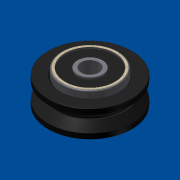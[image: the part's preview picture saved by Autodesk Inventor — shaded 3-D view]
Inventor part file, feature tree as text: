
AUTODESK INVENTOR PART (.ipt)
format: ipt  version: 2013 (Build 170138000, 138)  size: 254,464 bytes
history: native  units: in
note: dims shown in document units (in); Inventor stores cm internally (conversion verified against a paired STEP export)
features: other x6, extrude x2, sketch x2
ambient origin geometry x8: Origin, YZ Plane, XZ Plane, XY Plane, X Axis, Y Axis, Z Axis, Center Point
bodies: Solid1 (feature_tree)
feature tree (10):
  other  "MSK01-05A"
  other  "B17021.ipt:1"
  other  "BEARING_5_16_5.ipt:1"
  other  "BEARING_5_16_5.ipt:2"
  other  "MSK01-05A_Bodies"
  extrude  "Extrusion1"  Depth=0.0001in TaperAngle=0.0deg
  extrude  "Extrusion2"  [1 undecoded]
  other  "Srf1"
  sketch  "Sketch1"  dims[d0=0.3937in d1=0.0001in d2=0.0in]
  sketch  "Sketch2"  dims[d3=0.0001in d4=0.0in]
note: 1 required parameter value undecoded (feature->parameter linkage not recoverable at this tier; creation-order binding heuristic only, values carry confidence <= 0.55)
